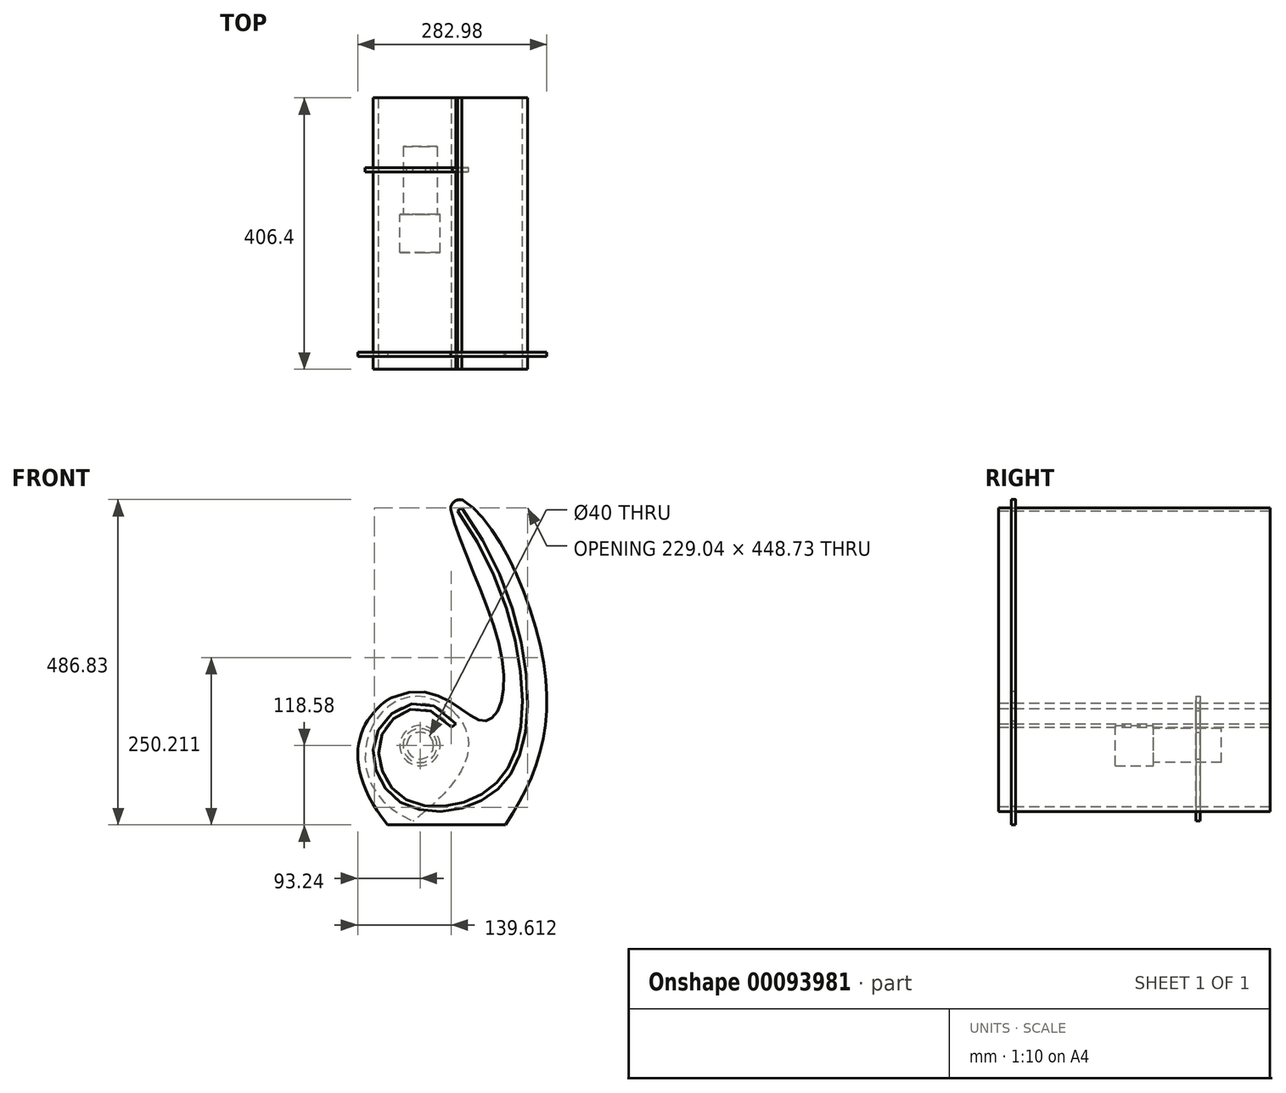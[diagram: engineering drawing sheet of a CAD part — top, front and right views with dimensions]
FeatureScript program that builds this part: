
annotation { "Feature Type Name" : "Feature", "Feature Type Description" : "" }
export const myFeature = defineFeature(function(context is Context, id is Id, definition is map)
    precondition{}
    {
        {
            var Q0;
            Q0=qCreatedBy(makeId("Front.planeOp"),FACE);
            var sketch = newSketch(context, id + "F0", { "sketchPlane" : qUnion([Q0])});
            skCircle(sketch, "E0", {"center": v(0, 0) * mm, "radius": 30.16 * mm});
            skSolve(sketch);
        }
        {
            var Q0;
            Q0=makeQuery(id+"F0.imprint","IMPRINT",FACE,{"disambiguationData":[TD([[makeQuery(id+"F0.imprint","IMPRINT",EDGE,{"derivedFrom":sQuery(id+"F0.wireOp",EDGE,"E0")}),1.0]])]});
            extrude(context, id + "F1", {"entities" : qUnion([Q0]), "depth" : 28.57 * mm, "hasSecondDirection" : true, "secondDirectionOppositeDirection" : true, "secondDirectionDepth" : 28.57 * mm});
        }
        {
            var Q0;
            Q0=qCreatedBy(makeId("Front.planeOp"),FACE);
            var sketch = newSketch(context, id + "F2", { "sketchPlane" : qUnion([Q0])});
            skCircle(sketch, "E1", {"center": v(0, 0) * mm, "radius": 25.4 * mm});
            skSolve(sketch);
        }
        {
            var Q0;
            Q0 = qSketchRegion(id + "F2", true);
            extrude(context, id + "F3", {"entities" : qUnion([Q0]), "operationType" : NewBodyOperationType.ADD, "oppositeDirection" : true, "depth" : 130.17 * mm});
        }
        {
            var Q0;
            Q0=qCreatedBy(makeId("Front.planeOp"),FACE);
            var sketch = newSketch(context, id + "F4", { "sketchPlane" : qUnion([Q0])});
            skFitSpline(sketch, "E2", {"points": [v(56.08, 351.56) * mm, v(150.76, 27.5) * mm, v(86.9, -76) * mm, v(-27.85, -76.3) * mm, v(-55.07, 20.2) * mm, v(47.32, 27.37) * mm], "startDerivative": vector(756.68, -1054.25) * mm, "endDerivative": vector(686.77, -871.03) * mm});
            skLineSegment(sketch, "E3", {"start": v(56.08, 351.56) * mm, "end": v(62.66, 356) * mm});
            skLineSegment(sketch, "E4", {"start": v(47.32, 27.37) * mm, "end": v(53.51, 32.34) * mm});
            skFitSpline(sketch, "E5", {"points": [v(53.51, 32.34) * mm, v(-62.28, 23.53) * mm, v(-33.21, -82.16) * mm, v(91.22, -82.67) * mm, v(158.43, 25.49) * mm, v(62.66, 356) * mm], "startDerivative": vector(-700.91, 948.41) * mm, "endDerivative": vector(-789.96, 1080.23) * mm});
            skLineSegment(sketch, "E6", {"start": v(-62.28, 23.53) * mm, "end": v(-55.07, 20.2) * mm, "construction": true});
            skLineSegment(sketch, "E7", {"start": v(-27.85, -76.3) * mm, "end": v(-33.21, -82.16) * mm, "construction": true});
            skLineSegment(sketch, "E8", {"start": v(86.9, -76) * mm, "end": v(91.22, -82.67) * mm, "construction": true});
            skLineSegment(sketch, "E9", {"start": v(150.76, 27.5) * mm, "end": v(158.43, 25.49) * mm, "construction": true});
            skSolve(sketch);
        }
        {
            var Q0;
            Q0 = qSketchRegion(id + "F4", true);
            extrude(context, id + "F5", {"entities" : qUnion([Q0]), "depth" : 203.2 * mm, "hasSecondDirection" : true, "secondDirectionOppositeDirection" : true, "secondDirectionDepth" : 203.2 * mm});
        }
        {
            var Q0;
            Q0=makeQuery(id+"F5.opExtrude","CAP_FACE",FACE,{"disambiguationData":[OSD([sQuery(id+"F4.wireOp",EDGE,"E2"),sQuery(id+"F4.wireOp",EDGE,"E3"),sQuery(id+"F4.wireOp",EDGE,"E4"),sQuery(id+"F4.wireOp",EDGE,"E5")])],"isStart":false});
            cPlane(context, id + "F6", {"entities" : qUnion([Q0]), "cplaneType" : CPlaneType.OFFSET, "offset" : 0 * mm, "width" : 152.4 * mm, "height" : 152.4 * mm});
        }
        {
            var Q0;
            Q0=qCreatedBy(id+"F6.planeOp",FACE);
            var sketch = newSketch(context, id + "F7", { "sketchPlane" : qUnion([Q0])});
            skFitSpline(sketch, "E10", {"points": [v(43.2, 375.02) * mm, v(123.94, 122.6) * mm, v(94.3, 36.76) * mm, v(-48.77, 68.44) * mm], "startDerivative": vector(6.41, -391.26) * mm, "endDerivative": vector(-698.64, -372.67) * mm});
            skFitSpline(sketch, "E11", {"points": [v(-48.77, 68.44) * mm, v(-48.62, -118.58) * mm], "startDerivative": vector(-144.68, -106.72) * mm, "endDerivative": vector(208.92, -263.66) * mm});
            skFitSpline(sketch, "E12", {"points": [v(43.2, 375.02) * mm, v(186.28, 114.42) * mm, v(128.03, -118.58) * mm], "startDerivative": vector(343.46, -40.75) * mm, "endDerivative": vector(-275.39, -425.6) * mm});
            skLineSegment(sketch, "E13", {"start": v(-48.62, -118.58) * mm, "end": v(128.03, -118.58) * mm});
            skSolve(sketch);
        }
        {
            var Q0;
            Q0 = qSketchRegion(id + "F7", true);
            extrude(context, id + "F8", {"entities" : qUnion([Q0]), "oppositeDirection" : true, "depth" : 25.4 * mm, "hasSecondDirection" : true, "secondDirectionOppositeDirection" : true, "secondDirectionDepth" : 19.05 * mm});
        }
        {
            var Q0;
            Q0=makeQuery(id+"F5.opExtrude","SWEPT_BODY",BODY,{"disambiguationData":[OSD([sQuery(id+"F4.wireOp",EDGE,"E2"),sQuery(id+"F4.wireOp",EDGE,"E3"),sQuery(id+"F4.wireOp",EDGE,"E4"),sQuery(id+"F4.wireOp",EDGE,"E5")])]});
            var Q1;
            Q1=makeQuery(id+"F8.opExtrude","SWEPT_BODY",BODY,{"disambiguationData":[OSD([sQuery(id+"F7.wireOp",EDGE,"E10"),sQuery(id+"F7.wireOp",EDGE,"E11"),sQuery(id+"F7.wireOp",EDGE,"E12"),sQuery(id+"F7.wireOp",EDGE,"E13")])]});
            booleanBodies(context, id + "F9", {"operationType" : BooleanOperationType.SUBTRACTION, "tools" : qUnion([Q0]), "targets" : qUnion([Q1]), "keepTools" : true});
        }
        {
            var Q0;
            Q0=makeQuery(id+"F8.opExtrude","SWEPT_EDGE",EDGE,{"disambiguationData":[OSD([sQuery(id+"F7.wireOp",EDGE,"E10"),sQuery(id+"F7.wireOp",EDGE,"E12")])]});
            fillet(context, id + "F10", {"entities" : qUnion([Q0]), "radius" : 12.7 * mm, "tangentPropagation" : true, "rho" : 0.25, "crossSection" : FilletCrossSection.CONIC, "allowEdgeOverflow" : false});
        }
        {
            var Q0;
            Q0=makeQuery(id+"F8.opExtrude","SWEPT_EDGE",EDGE,{"disambiguationData":[OSD([sQuery(id+"F7.wireOp",EDGE,"E10"),sQuery(id+"F7.wireOp",EDGE,"E11")])]});
            fillet(context, id + "F11", {"entities" : qUnion([Q0]), "radius" : 50.8 * mm, "tangentPropagation" : true, "allowEdgeOverflow" : false});
        }
        {
            var Q0;
            Q0=makeQuery(id+"F1.opExtrude","CAP_FACE",FACE,{"disambiguationData":[OSD([sQuery(id+"F0.wireOp",EDGE,"E0")])],"isStart":false});
            cPlane(context, id + "F12", {"entities" : qUnion([Q0]), "cplaneType" : CPlaneType.OFFSET, "offset" : 127 * mm, "oppositeDirection" : true, "width" : 152.4 * mm, "height" : 152.4 * mm});
        }
        {
            var Q0;
            Q0=qCreatedBy(id+"F12.planeOp",FACE);
            var sketch = newSketch(context, id + "F13", { "sketchPlane" : qUnion([Q0])});
            skFitSpline(sketch, "E14", {"points": [v(48.7, 52.33) * mm, v(-10.69, -113) * mm], "startDerivative": vector(-313.05, 252.46) * mm, "endDerivative": vector(428.43, -183.8) * mm});
            skCircle(sketch, "E15", {"center": v(0, 0) * mm, "radius": 20 * mm});
            skFitSpline(sketch, "E16", {"points": [v(48.7, 52.33) * mm, v(-10.69, -113) * mm], "startDerivative": vector(211.58, -211.06) * mm, "endDerivative": vector(-68.76, -56.86) * mm});
            skSolve(sketch);
        }
        {
            var Q0;
            Q0 = qSketchRegion(id + "F13", true);
            extrude(context, id + "F14", {"entities" : qUnion([Q0]), "depth" : 6.35 * mm});
        }
        {
            var Q0;
            Q0=makeQuery(id+"F5.opExtrude","SWEPT_BODY",BODY,{"disambiguationData":[OSD([sQuery(id+"F4.wireOp",EDGE,"E2"),sQuery(id+"F4.wireOp",EDGE,"E3"),sQuery(id+"F4.wireOp",EDGE,"E4"),sQuery(id+"F4.wireOp",EDGE,"E5")])]});
            var Q1;
            Q1=makeQuery(id+"F14.opExtrude","SWEPT_BODY",BODY,{"disambiguationData":[OSD([sQuery(id+"F13.wireOp",EDGE,"E14"),sQuery(id+"F13.wireOp",EDGE,"E15"),sQuery(id+"F13.wireOp",EDGE,"E16")])]});
            booleanBodies(context, id + "F15", {"operationType" : BooleanOperationType.SUBTRACTION, "tools" : qUnion([Q0]), "targets" : qUnion([Q1]), "keepTools" : true});
        }
        {
            var Q0;
            Q0=makeQuery(id+"F1.opExtrude","SWEPT_BODY",BODY,{"disambiguationData":[OSD([sQuery(id+"F0.wireOp",EDGE,"E0")])]});
            transform(context, id + "F16", {"entities" : qUnion([Q0]), "transformType" : TransformType.TRANSLATION_3D, "dx" : 0 * mm, "dy" : 0 * mm, "dz" : 0 * mm, "makeCopy" : true});
        }
        {
            var Q0;
            Q0=makeQuery(id+"F16.opPattern","COPY",BODY,{"derivedFrom":makeQuery(id+"F1.opExtrude","SWEPT_BODY",BODY,{"disambiguationData":[OSD([sQuery(id+"F0.wireOp",EDGE,"E0")])]}),"instanceName":"1"});
            deleteBodies(context, id + "F17", {"entities" : qUnion([Q0])});
        }
    });
